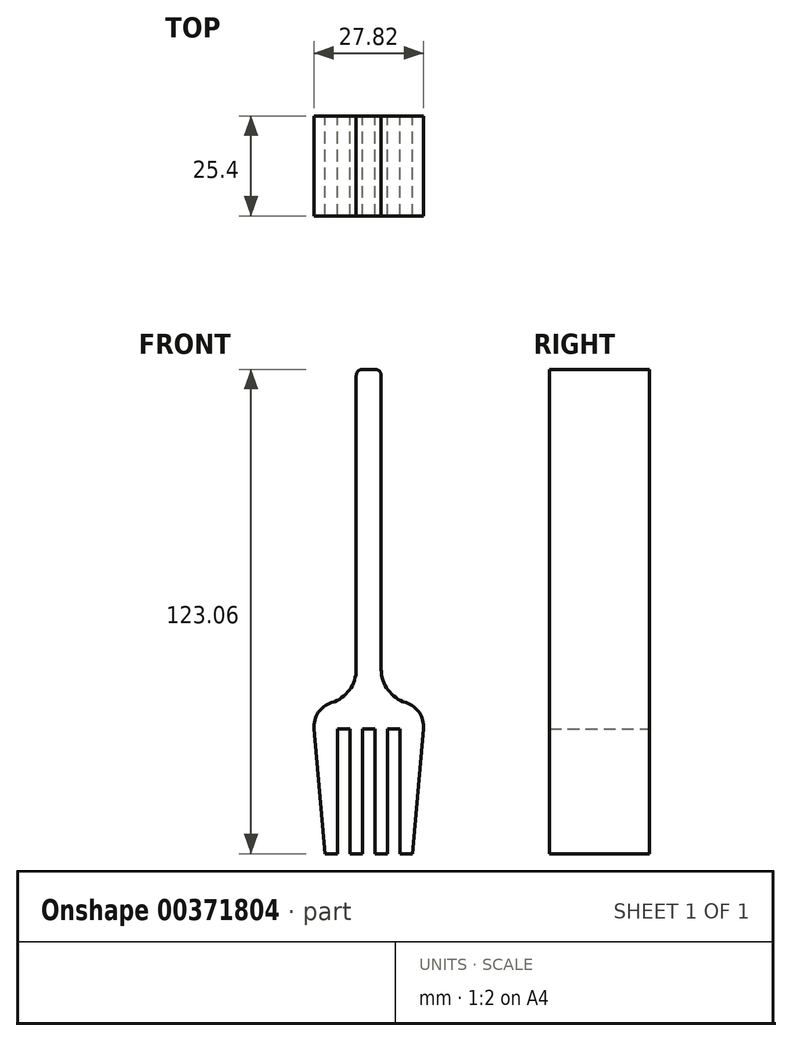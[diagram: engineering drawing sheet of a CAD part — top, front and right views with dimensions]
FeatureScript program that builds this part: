
annotation { "Feature Type Name" : "Feature", "Feature Type Description" : "" }
export const myFeature = defineFeature(function(context is Context, id is Id, definition is map)
    precondition{}
    {
        {
            var Q0;
            Q0=qCreatedBy(makeId("Front.planeOp"),FACE);
            var sketch = newSketch(context, id + "F0", { "sketchPlane" : qUnion([Q0])});
            skLineSegment(sketch, "E0", {"start": v(-3.18, 74.61) * mm, "end": v(-3.17, 0) * mm});
            skArc(sketch, "E1", {"start": v(-1.59, 76.2) * mm, "mid": v(-2.71, 75.74) * mm, "end": v(-3.18, 74.61) * mm});
            skLineSegment(sketch, "E2", {"start": v(-1.59, 76.2) * mm, "end": v(0, 76.2) * mm});
            skArc(sketch, "E3", {"start": v(-9.44, -8.5) * mm, "mid": v(-4.91, -5.28) * mm, "end": v(-3.17, 0) * mm});
            skArc(sketch, "E4", {"start": v(-9.44, -8.5) * mm, "mid": v(-12.83, -11.02) * mm, "end": v(-13.9, -15.11) * mm});
            skLineSegment(sketch, "E5", {"start": v(-13.9, -15.11) * mm, "end": v(-11.11, -46.86) * mm});
            skLineSegment(sketch, "E6", {"start": v(-11.11, -46.86) * mm, "end": v(-7.94, -46.86) * mm});
            skLineSegment(sketch, "E7", {"start": v(-7.94, -46.86) * mm, "end": v(-7.94, -15.11) * mm});
            skLineSegment(sketch, "E8", {"start": v(-7.94, -15.11) * mm, "end": v(-4.76, -15.11) * mm});
            skLineSegment(sketch, "E9", {"start": v(-4.76, -15.11) * mm, "end": v(-4.76, -46.86) * mm});
            skPoint(sketch, "E10.end.orphan", {"position": v(0, -15.11) * mm});
            skPoint(sketch, "E11.end.orphan", {"position": v(0, -38.82) * mm});
            skLineSegment(sketch, "E12", {"start": v(0, 71.5) * mm, "end": v(0, -78.6) * mm, "construction": true});
            skLineSegment(sketch, "E13", {"start": v(-4.76, -46.86) * mm, "end": v(-1.59, -46.86) * mm});
            skLineSegment(sketch, "E14", {"start": v(-1.59, -46.86) * mm, "end": v(-1.59, -15.11) * mm});
            skLineSegment(sketch, "E15", {"start": v(-1.59, -15.11) * mm, "end": v(0, -15.11) * mm});
            skLineSegment(sketch, "E16.MirrorCS", {"start": v(4.76, -46.86) * mm, "end": v(1.59, -46.86) * mm});
            skLineSegment(sketch, "E17.MirrorCS", {"start": v(7.94, -15.11) * mm, "end": v(4.76, -15.11) * mm});
            skArc(sketch, "E18.MirrorCS", {"start": v(9.44, -8.5) * mm, "mid": v(4.91, -5.28) * mm, "end": v(3.18, 0) * mm});
            skArc(sketch, "E19.MirrorCS", {"start": v(9.44, -8.5) * mm, "mid": v(12.83, -11.02) * mm, "end": v(13.9, -15.11) * mm});
            skLineSegment(sketch, "E20.MirrorCS", {"start": v(11.11, -46.86) * mm, "end": v(7.94, -46.86) * mm});
            skArc(sketch, "E21.MirrorCS", {"start": v(1.59, 76.2) * mm, "mid": v(2.71, 75.74) * mm, "end": v(3.18, 74.61) * mm});
            skLineSegment(sketch, "E22.MirrorCS", {"start": v(1.59, -46.86) * mm, "end": v(1.59, -15.11) * mm});
            skLineSegment(sketch, "E23.MirrorCS", {"start": v(3.18, 74.61) * mm, "end": v(3.17, 0) * mm});
            skLineSegment(sketch, "E24.MirrorCS", {"start": v(4.76, -15.11) * mm, "end": v(4.76, -46.86) * mm});
            skLineSegment(sketch, "E25.MirrorCS", {"start": v(13.9, -15.11) * mm, "end": v(11.11, -46.86) * mm});
            skLineSegment(sketch, "E26.MirrorCS", {"start": v(7.94, -46.86) * mm, "end": v(7.94, -15.11) * mm});
            skLineSegment(sketch, "E27.MirrorCS", {"start": v(1.59, 76.2) * mm, "end": v(0, 76.2) * mm});
            skLineSegment(sketch, "E28.MirrorCS", {"start": v(1.59, -15.11) * mm, "end": v(0, -15.11) * mm});
            skSolve(sketch);
        }
        {
            var Q0;
            Q0 = qSketchRegion(id + "F0", true);
            extrude(context, id + "F1", {"entities" : qUnion([Q0]), "depth" : 25.4 * mm});
        }
    });
